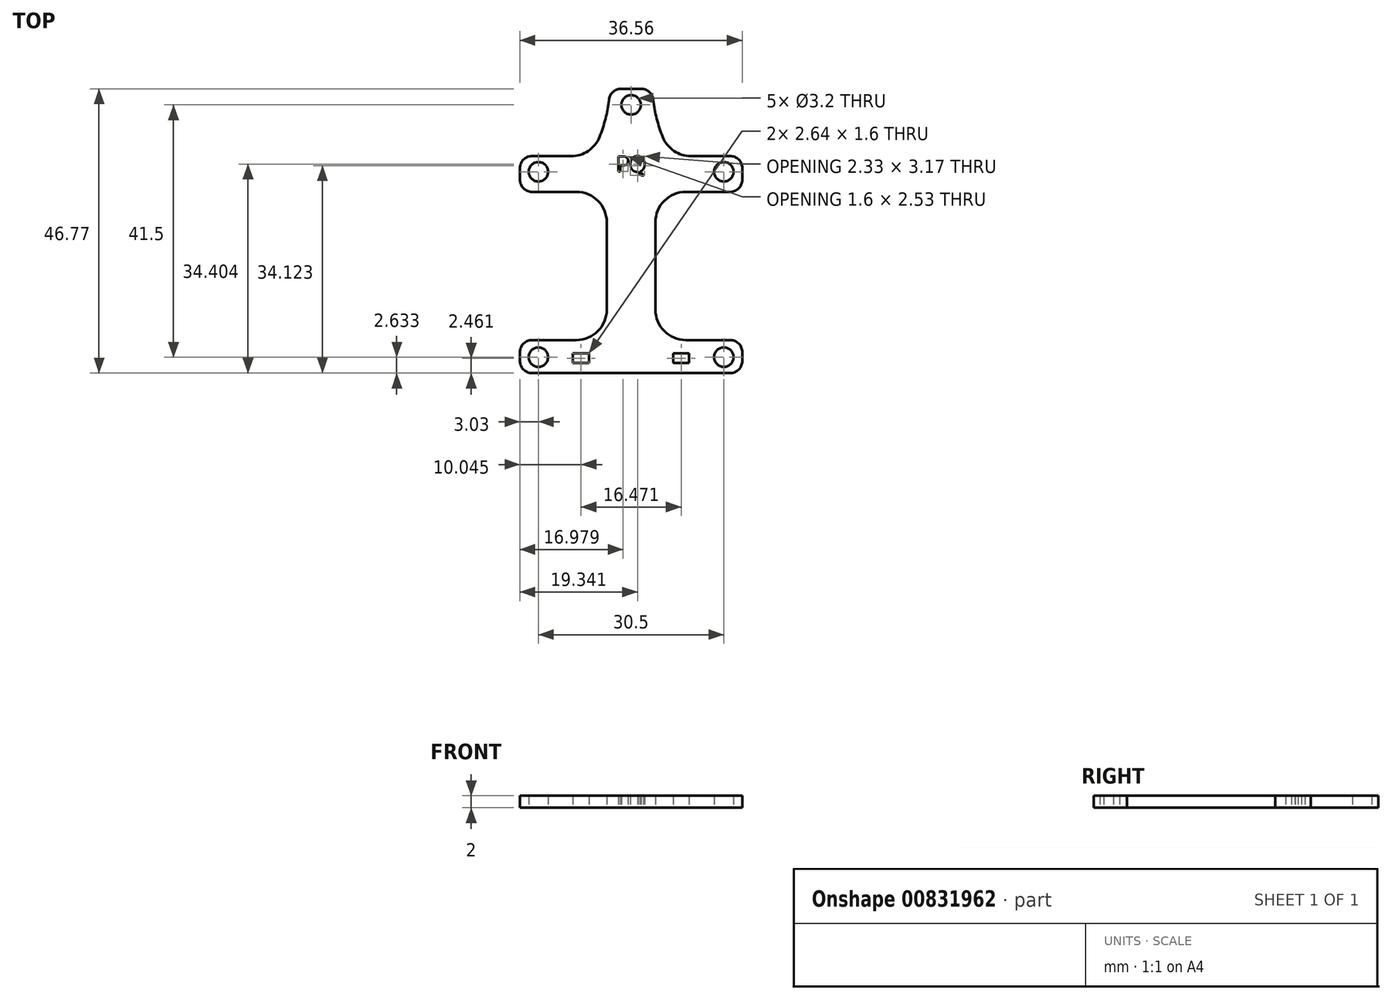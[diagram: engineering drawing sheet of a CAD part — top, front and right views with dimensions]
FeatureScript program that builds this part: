
annotation { "Feature Type Name" : "Feature", "Feature Type Description" : "" }
export const myFeature = defineFeature(function(context is Context, id is Id, definition is map)
    precondition{}
    {
        {
            var Q0;
            Q0=qCreatedBy(makeId("Top.planeOp"),FACE);
            var sketch = newSketch(context, id + "F0", { "sketchPlane" : qUnion([Q0])});
            skCircle(sketch, "E0.MirrorC", {"center": v(13.1, 8.4) * mm, "radius": 1.6 * mm});
            skCircle(sketch, "E1.MirrorC", {"center": v(43.6, 8.4) * mm, "radius": 1.6 * mm});
            skCircle(sketch, "E2.MirrorC", {"center": v(43.6, 38.9) * mm, "radius": 1.6 * mm});
            skCircle(sketch, "E3.MirrorC", {"center": v(13.1, 38.9) * mm, "radius": 1.6 * mm});
            skPoint(sketch, "E4", {"position": v(28.35, 38.9) * mm});
            skPoint(sketch, "E5.orphan", {"position": v(15.2, 38.07) * mm});
            skPoint(sketch, "E6.orphan", {"position": v(14.92, 50.26) * mm});
            skPoint(sketch, "E7.MirrorP", {"position": v(39.77, 55.59) * mm});
            skPoint(sketch, "E8.MirrorP", {"position": v(40.3, 38.07) * mm});
            skPoint(sketch, "E9", {"position": v(28.35, 49.9) * mm});
            skCircle(sketch, "E10", {"center": v(28.35, 49.9) * mm, "radius": 1.6 * mm});
            skPoint(sketch, "E11", {"position": v(32.85, 51.82) * mm});
            skPoint(sketch, "E12", {"position": v(40.85, 51.82) * mm});
            skPoint(sketch, "E13", {"position": v(43.6, 23.65) * mm});
            skLineSegment(sketch, "E14.left", {"start": v(10.07, 40.38) * mm, "end": v(10.07, 35.6) * mm});
            skLineSegment(sketch, "E14.right", {"start": v(46.63, 40.38) * mm, "end": v(46.63, 35.6) * mm});
            skPoint(sketch, "E15.orphan", {"position": v(46.63, 65.65) * mm});
            skPoint(sketch, "E16.orphan", {"position": v(10.07, 65.65) * mm});
            skPoint(sketch, "E17.orphan", {"position": v(10.07, -18.35) * mm});
            skPoint(sketch, "E18.orphan", {"position": v(46.63, -18.35) * mm});
            skLineSegment(sketch, "E19", {"start": v(28.35, 23.65) * mm, "end": v(28.35, 32.54) * mm});
            skLineSegment(sketch, "E20.left", {"start": v(28.35, 12.7) * mm, "end": v(28.35, 10.6) * mm});
            skLineSegment(sketch, "E21.MirrorCS", {"start": v(28.35, 38.83) * mm, "end": v(28.35, 36.73) * mm});
            skPoint(sketch, "E22.MirrorP", {"position": v(13.1, 23.65) * mm});
            skPoint(sketch, "E23.MirrorP", {"position": v(16.4, 38.07) * mm});
            skLineSegment(sketch, "E24", {"start": v(28.35, 38.9) * mm, "end": v(28.35, 10.6) * mm});
            skLineSegment(sketch, "E25.0", {"start": v(24.35, 30.6) * mm, "end": v(24.35, 16.22) * mm});
            skLineSegment(sketch, "E26", {"start": v(46.63, 35.6) * mm, "end": v(37.35, 35.6) * mm});
            skLineSegment(sketch, "E27.MirrorCS", {"start": v(10.07, 35.6) * mm, "end": v(19.35, 35.6) * mm});
            skLineSegment(sketch, "E28.trimOffspring", {"start": v(46.63, 11.22) * mm, "end": v(46.63, 5.77) * mm});
            skLineSegment(sketch, "E29.trimOffspring", {"start": v(10.07, 11.22) * mm, "end": v(10.07, 5.77) * mm});
            skPoint(sketch, "E30.MirrorCS.endDerivative.orphan", {"position": v(34.48, 2.5) * mm});
            skPoint(sketch, "E31.1.internal.orphan", {"position": v(13.1, 0) * mm});
            skPoint(sketch, "E32.end.orphan", {"position": v(34.48, 4.76) * mm});
            skPoint(sketch, "E33.start.orphan", {"position": v(39.57, 2.5) * mm});
            skPoint(sketch, "E34.0.internal.orphan", {"position": v(28.35, 41.06) * mm});
            skPoint(sketch, "E34.2.internal.orphan", {"position": v(28.35, 45.5) * mm});
            skPoint(sketch, "E35.3.internal.orphan", {"position": v(28.35, 53.53) * mm});
            skLineSegment(sketch, "E36", {"start": v(28.35, 52.54) * mm, "end": v(24.83, 52.54) * mm});
            skLineSegment(sketch, "E37.MirrorCS", {"start": v(28.35, 52.54) * mm, "end": v(31.87, 52.54) * mm});
            skLineSegment(sketch, "E38", {"start": v(10.07, 40.38) * mm, "end": v(10.07, 41.48) * mm});
            skLineSegment(sketch, "E39", {"start": v(10.07, 41.48) * mm, "end": v(18.52, 41.48) * mm});
            skArc(sketch, "E40", {"start": v(23.15, 44.6) * mm, "mid": v(24.34, 48.5) * mm, "end": v(24.83, 52.54) * mm});
            skArc(sketch, "E41.MirrorCS", {"start": v(33.55, 44.6) * mm, "mid": v(32.36, 48.5) * mm, "end": v(31.87, 52.54) * mm});
            skLineSegment(sketch, "E42.MirrorCS", {"start": v(46.63, 41.48) * mm, "end": v(38.18, 41.48) * mm});
            skLineSegment(sketch, "E43.MirrorCS", {"start": v(46.63, 40.38) * mm, "end": v(46.63, 41.48) * mm});
            skLineSegment(sketch, "E44", {"start": v(46.63, 11.22) * mm, "end": v(37.35, 11.22) * mm});
            skLineSegment(sketch, "E45", {"start": v(46.63, 5.77) * mm, "end": v(10.07, 5.77) * mm});
            skPoint(sketch, "E46.MirrorCS.end.orphan", {"position": v(32.35, 13.91) * mm});
            skPoint(sketch, "E47.orphan", {"position": v(46.63, 13.91) * mm});
            skLineSegment(sketch, "E48.MirrorCS", {"start": v(10.07, 11.22) * mm, "end": v(19.35, 11.22) * mm});
            skPoint(sketch, "E49.MirrorCS.end.orphan", {"position": v(24.35, 13.91) * mm});
            skPoint(sketch, "E50.orphan", {"position": v(10.07, 13.91) * mm});
            skPoint(sketch, "E51.start.orphan", {"position": v(32.35, 24.75) * mm});
            skLineSegment(sketch, "E52.bottom", {"start": v(18.8, 7.43) * mm, "end": v(21.44, 7.43) * mm});
            skLineSegment(sketch, "E52.top", {"start": v(18.8, 9.03) * mm, "end": v(21.44, 9.03) * mm});
            skLineSegment(sketch, "E52.left", {"start": v(18.8, 7.43) * mm, "end": v(18.8, 9.03) * mm});
            skLineSegment(sketch, "E52.right", {"start": v(21.44, 7.43) * mm, "end": v(21.44, 9.03) * mm});
            skLineSegment(sketch, "E53.MirrorCS", {"start": v(35.26, 7.43) * mm, "end": v(35.26, 9.03) * mm});
            skLineSegment(sketch, "E54.MirrorCS", {"start": v(37.9, 7.43) * mm, "end": v(35.26, 7.43) * mm});
            skLineSegment(sketch, "E55.MirrorCS", {"start": v(37.9, 9.03) * mm, "end": v(35.26, 9.03) * mm});
            skLineSegment(sketch, "E56.MirrorCS", {"start": v(37.9, 7.43) * mm, "end": v(37.9, 9.03) * mm});
            skPoint(sketch, "E57.newPointA", {"position": v(24.35, 35.6) * mm});
            skArc(sketch, "E57.filletArc", {"start": v(24.35, 30.6) * mm, "mid": v(22.89, 34.13) * mm, "end": v(19.35, 35.6) * mm});
            skLineSegment(sketch, "E58", {"start": v(32.35, 24.75) * mm, "end": v(38, 24.75) * mm});
            skArc(sketch, "E59.MirrorCS", {"start": v(32.35, 30.6) * mm, "mid": v(33.81, 34.13) * mm, "end": v(37.35, 35.6) * mm});
            skPoint(sketch, "E60.newPointA", {"position": v(24.35, 11.22) * mm});
            skArc(sketch, "E60.filletArc", {"start": v(19.35, 11.22) * mm, "mid": v(22.89, 12.69) * mm, "end": v(24.35, 16.22) * mm});
            skArc(sketch, "E61.MirrorCS", {"start": v(37.35, 11.22) * mm, "mid": v(33.81, 12.69) * mm, "end": v(32.35, 16.22) * mm});
            skLineSegment(sketch, "E62.trimOffspring", {"start": v(32.35, 11.22) * mm, "end": v(32.35, 10.6) * mm});
            skLineSegment(sketch, "E63.trimOffspring", {"start": v(32.35, 30.6) * mm, "end": v(32.35, 13.91) * mm});
            skPoint(sketch, "E64.0.start.orphan", {"position": v(32.35, 38.9) * mm});
            skPoint(sketch, "E65.orphan", {"position": v(32.35, 35.6) * mm});
            skPoint(sketch, "E66.visualSharp", {"position": v(35.1, 41.48) * mm});
            skArc(sketch, "E66.filletArc", {"start": v(33.55, 44.6) * mm, "mid": v(35.39, 42.33) * mm, "end": v(38.18, 41.48) * mm});
            skArc(sketch, "E67.MirrorCS", {"start": v(23.15, 44.6) * mm, "mid": v(21.31, 42.33) * mm, "end": v(18.52, 41.48) * mm});
            skPoint(sketch, "E68.orphan", {"position": v(21.6, 41.48) * mm});
            skText(sketch, "E69", { "text": "PQ", "fontName": "OpenSans-Regular.ttf"});
            const initialGuessF0  = {"E69": [0.0259, 0.03891, 1, 0, 0.00255]};
            skSetInitialGuess(sketch, initialGuessF0);
            skSolve(sketch);
        }
        {
            var Q0;
            Q0=makeQuery(id+"F0.imprint","IMPRINT",FACE,{"disambiguationData":[TD([[makeQuery(id+"F0.imprint","IMPRINT",EDGE,{"derivedFrom":sQuery(id+"F0.wireOp",EDGE,"E0.MirrorC")}),-1.0]])]});
            extrude(context, id + "F1", {"entities" : qUnion([Q0]), "depth" : 2 * mm, "offsetDistance" : 25 * mm});
        }
        {
            var Q0;
            Q0=makeQuery(id+"F1.opExtrude","SWEPT_EDGE",EDGE,{"disambiguationData":[OSD([sQuery(id+"F0.wireOp",EDGE,"E28.trimOffspring"),sQuery(id+"F0.wireOp",EDGE,"E45")])]});
            var Q1;
            Q1=makeQuery(id+"F1.opExtrude","SWEPT_EDGE",EDGE,{"disambiguationData":[OSD([sQuery(id+"F0.wireOp",EDGE,"E29.trimOffspring"),sQuery(id+"F0.wireOp",EDGE,"E45")])]});
            var Q2;
            Q2=makeQuery(id+"F1.opExtrude","SWEPT_EDGE",EDGE,{"disambiguationData":[OSD([sQuery(id+"F0.wireOp",EDGE,"E14.left"),sQuery(id+"F0.wireOp",EDGE,"E27.MirrorCS")])]});
            var Q3;
            Q3=makeQuery(id+"F1.opExtrude","SWEPT_EDGE",EDGE,{"disambiguationData":[OSD([sQuery(id+"F0.wireOp",EDGE,"E14.right"),sQuery(id+"F0.wireOp",EDGE,"E26")])]});
            fillet(context, id + "F2", {"entities" : qUnion([Q0, Q1, Q2, Q3]), "radius" : 2 * mm, "tangentPropagation" : true, "allowEdgeOverflow" : false});
        }
        {
            var Q0;
            Q0=makeQuery(id+"F1.opExtrude","SWEPT_EDGE",EDGE,{"disambiguationData":[OSD([sQuery(id+"F0.wireOp",EDGE,"E38"),sQuery(id+"F0.wireOp",EDGE,"E39")])]});
            var Q1;
            Q1=makeQuery(id+"F1.opExtrude","SWEPT_EDGE",EDGE,{"disambiguationData":[OSD([sQuery(id+"F0.wireOp",EDGE,"E42.MirrorCS"),sQuery(id+"F0.wireOp",EDGE,"E43.MirrorCS")])]});
            var Q2;
            Q2=makeQuery(id+"F1.opExtrude","SWEPT_EDGE",EDGE,{"disambiguationData":[OSD([sQuery(id+"F0.wireOp",EDGE,"E28.trimOffspring"),sQuery(id+"F0.wireOp",EDGE,"E44")])]});
            var Q3;
            Q3=makeQuery(id+"F1.opExtrude","SWEPT_EDGE",EDGE,{"disambiguationData":[OSD([sQuery(id+"F0.wireOp",EDGE,"E29.trimOffspring"),sQuery(id+"F0.wireOp",EDGE,"E48.MirrorCS")])]});
            var Q4;
            Q4=makeQuery(id+"F1.opExtrude","SWEPT_EDGE",EDGE,{"disambiguationData":[OSD([sQuery(id+"F0.wireOp",EDGE,"E36"),sQuery(id+"F0.wireOp",EDGE,"E40")])]});
            var Q5;
            Q5=makeQuery(id+"F1.opExtrude","SWEPT_EDGE",EDGE,{"disambiguationData":[OSD([sQuery(id+"F0.wireOp",EDGE,"E37.MirrorCS"),sQuery(id+"F0.wireOp",EDGE,"E41.MirrorCS")])]});
            fillet(context, id + "F3", {"entities" : qUnion([Q0, Q1, Q2, Q3, Q4, Q5]), "radius" : 2 * mm, "tangentPropagation" : true, "allowEdgeOverflow" : false});
        }
    });
